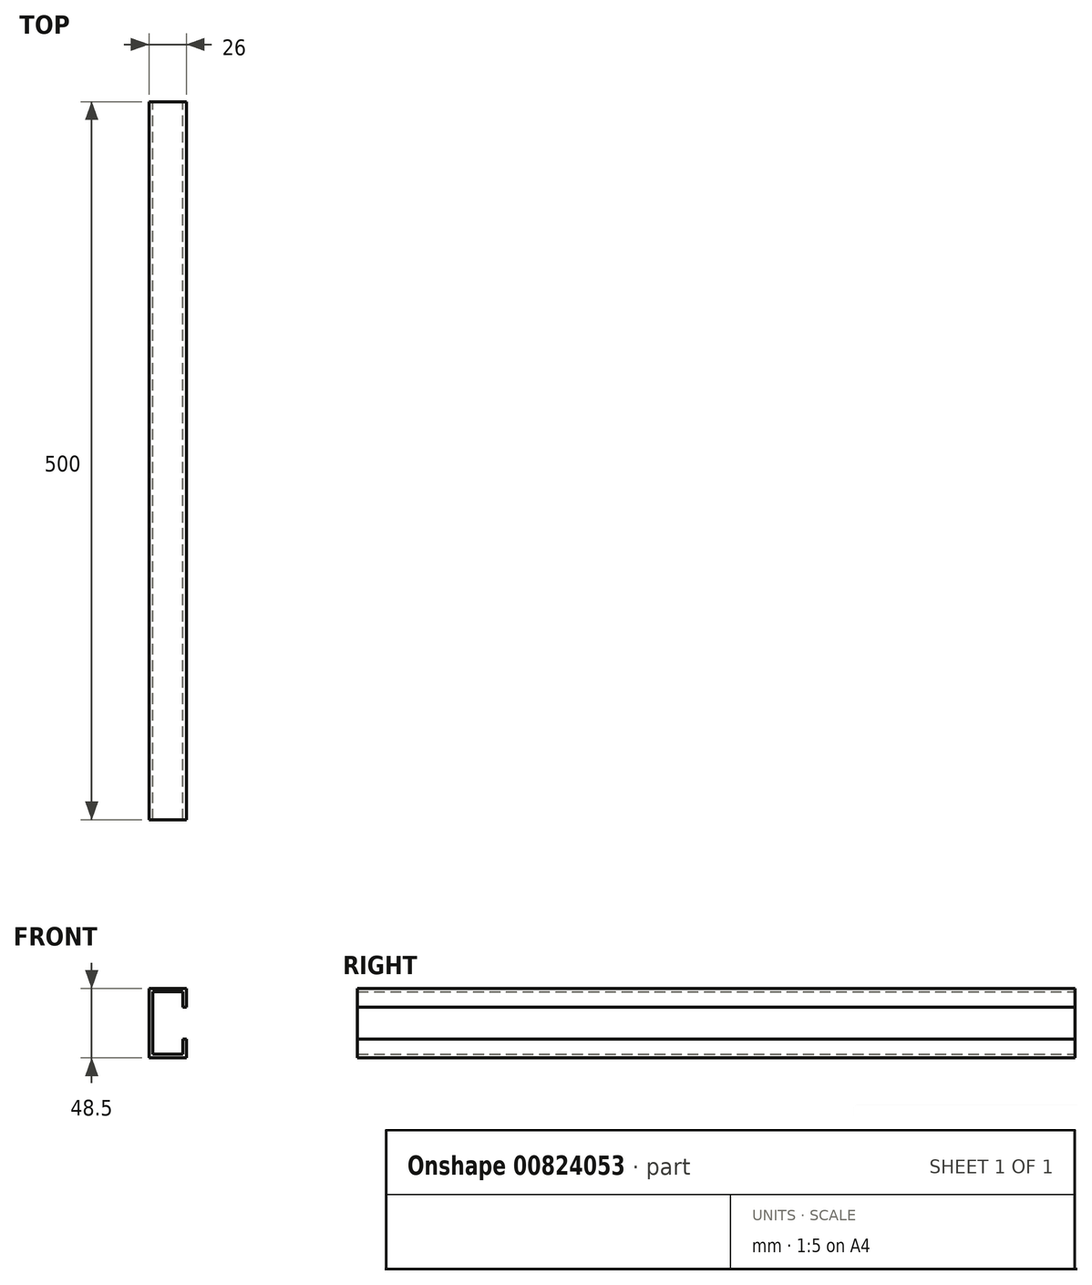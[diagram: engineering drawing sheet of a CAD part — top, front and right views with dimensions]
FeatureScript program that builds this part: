
annotation { "Feature Type Name" : "Feature", "Feature Type Description" : "" }
export const myFeature = defineFeature(function(context is Context, id is Id, definition is map)
    precondition{}
    {
        {
            var Q0;
            Q0=qCreatedBy(makeId("Front.planeOp"),FACE);
            var sketch = newSketch(context, id + "F0", { "sketchPlane" : qUnion([Q0])});
            skLineSegment(sketch, "E0.bottom", {"start": v(0, 24.25) * mm, "end": v(26, 24.25) * mm});
            skLineSegment(sketch, "E0.top", {"start": v(0, -24.25) * mm, "end": v(26, -24.25) * mm});
            skLineSegment(sketch, "E0.left", {"start": v(0, 24.25) * mm, "end": v(0, -24.25) * mm});
            skLineSegment(sketch, "E0.right", {"start": v(26, 24.25) * mm, "end": v(26, -24.25) * mm});
            skPoint(sketch, "E0.middle", {"position": v(13, 0) * mm});
            skSolve(sketch);
        }
        {
            var Q0;
            Q0=qCreatedBy(makeId("Front.planeOp"),FACE);
            var sketch = newSketch(context, id + "F1", { "sketchPlane" : qUnion([Q0])});
            skLineSegment(sketch, "E1.bottom", {"start": v(23.5, 21.75) * mm, "end": v(2.5, 21.75) * mm});
            skLineSegment(sketch, "E1.top", {"start": v(23.5, -21.75) * mm, "end": v(2.5, -21.75) * mm});
            skLineSegment(sketch, "E1.left", {"start": v(23.5, 21.75) * mm, "end": v(23.5, 11.25) * mm});
            skLineSegment(sketch, "E1.right", {"start": v(2.5, 21.75) * mm, "end": v(2.5, -21.75) * mm});
            skPoint(sketch, "E1.middle", {"position": v(13, 0) * mm});
            skLineSegment(sketch, "E2.0", {"start": v(26, 24.25) * mm, "end": v(26, -24.25) * mm, "construction": true});
            skLineSegment(sketch, "E3", {"start": v(23.5, 11.25) * mm, "end": v(26, 11.25) * mm});
            skLineSegment(sketch, "E4", {"start": v(26, 11.25) * mm, "end": v(26, -11.25) * mm});
            skLineSegment(sketch, "E5", {"start": v(26, -11.25) * mm, "end": v(23.5, -11.25) * mm});
            skLineSegment(sketch, "E6.trimOffspring", {"start": v(23.5, -11.25) * mm, "end": v(23.5, -21.75) * mm});
            skSolve(sketch);
        }
        {
            var Q0;
            Q0=makeQuery(id+"F0.imprint","IMPRINT",FACE,{"disambiguationData":[TD([[makeQuery(id+"F0.imprint","IMPRINT",EDGE,{"derivedFrom":sQuery(id+"F0.wireOp",EDGE,"E0.bottom")}),-1.0]])]});
            extrude(context, id + "F2", {"entities" : qUnion([Q0]), "depth" : 500 * mm, "offsetDistance" : 25 * mm});
        }
        {
            var Q0;
            Q0=makeQuery(id+"F1.imprint","IMPRINT",FACE,{"disambiguationData":[TD([[makeQuery(id+"F1.imprint","IMPRINT",EDGE,{"derivedFrom":sQuery(id+"F1.wireOp",EDGE,"E1.bottom")}),1.0]])]});
            extrude(context, id + "F3", {"entities" : qUnion([Q0]), "operationType" : NewBodyOperationType.REMOVE, "endBound" : BoundingType.UP_TO_NEXT, "depth" : 25 * mm, "offsetDistance" : 25 * mm});
        }
    });
